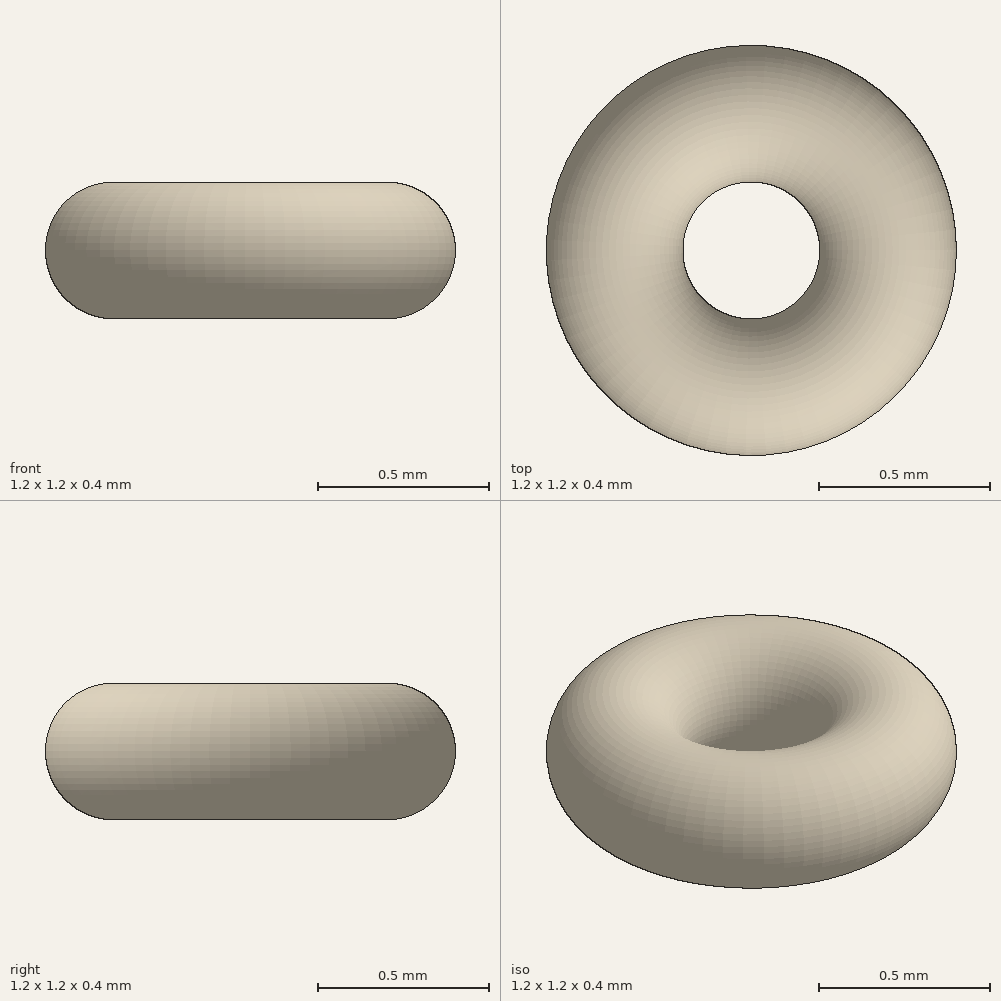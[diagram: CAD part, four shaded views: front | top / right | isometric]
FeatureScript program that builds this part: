
annotation { "Feature Type Name" : "Feature", "Feature Type Description" : "" }
export const myFeature = defineFeature(function(context is Context, id is Id, definition is map)
    precondition{}
    {
        {
            var Q0;
            Q0=qCreatedBy(makeId("Top.planeOp"),FACE);
            cPlane(context, id + "F0", {"entities" : qUnion([Q0]), "cplaneType" : CPlaneType.OFFSET, "offset" : 0.2 * mm, "width" : 150 * mm, "height" : 150 * mm});
        }
        {
            var Q0;
            Q0=qCreatedBy(id+"F0.planeOp",FACE);
            var sketch = newSketch(context, id + "F1", { "sketchPlane" : qUnion([Q0])});
            skLineSegment(sketch, "E0.bottom", {"start": v(10, 10) * mm, "end": v(-10, 10) * mm});
            skLineSegment(sketch, "E0.top", {"start": v(10, -10) * mm, "end": v(-10, -10) * mm});
            skLineSegment(sketch, "E0.right", {"start": v(-10, 9.6) * mm, "end": v(-10, -10) * mm});
            skPoint(sketch, "E0.middle", {"position": v(0, 0) * mm});
            skLineSegment(sketch, "E1", {"start": v(-9.6, 10) * mm, "end": v(-9.6, 10) * mm});
            skLineSegment(sketch, "E2", {"start": v(-9.2, 9.6) * mm, "end": v(-9.2, -9.6) * mm});
            skLineSegment(sketch, "E3", {"start": v(-9.2, -10) * mm, "end": v(-10, -10) * mm});
            skLineSegment(sketch, "E4", {"start": v(-9.2, 10) * mm, "end": v(-8.4, 10) * mm});
            skLineSegment(sketch, "E5", {"start": v(-8.4, 10) * mm, "end": v(-8.4, -9.6) * mm});
            skLineSegment(sketch, "E6", {"start": v(-8.8, -10) * mm, "end": v(-8.8, -10) * mm});
            skPoint(sketch, "E7.visualSharp", {"position": v(-10, 10) * mm});
            skArc(sketch, "E7.filletArc", {"start": v(-9.6, 10) * mm, "mid": v(-9.88, 9.88) * mm, "end": v(-10, 9.6) * mm});
            skPoint(sketch, "E8.visualSharp", {"position": v(-9.2, 10) * mm});
            skArc(sketch, "E8.filletArc", {"start": v(-9.2, 9.6) * mm, "mid": v(-9.32, 9.88) * mm, "end": v(-9.6, 10) * mm});
            skPoint(sketch, "E9.visualSharp", {"position": v(-9.2, -10) * mm});
            skArc(sketch, "E9.filletArc", {"start": v(-9.2, -9.6) * mm, "mid": v(-9.08, -9.88) * mm, "end": v(-8.8, -10) * mm});
            skPoint(sketch, "E10.visualSharp", {"position": v(-8.4, -10) * mm});
            skArc(sketch, "E10.filletArc", {"start": v(-8.8, -10) * mm, "mid": v(-8.52, -9.88) * mm, "end": v(-8.4, -9.6) * mm});
            skLineSegment(sketch, "E11", {"start": v(-8.4, 9.6) * mm, "end": v(-8.4, -9.6) * mm});
            skArc(sketch, "E12.1.0.0", {"start": v(-8, 10) * mm, "mid": v(-8.28, 9.88) * mm, "end": v(-8.4, 9.6) * mm});
            skArc(sketch, "E12.1.0.1", {"start": v(-7.6, 9.6) * mm, "mid": v(-7.72, 9.88) * mm, "end": v(-8, 10) * mm});
            skLineSegment(sketch, "E12.1.0.2", {"start": v(-7.6, 9.6) * mm, "end": v(-7.6, -9.6) * mm});
            skArc(sketch, "E12.1.0.3", {"start": v(-7.6, -9.6) * mm, "mid": v(-7.48, -9.88) * mm, "end": v(-7.2, -10) * mm});
            skArc(sketch, "E12.1.0.4", {"start": v(-7.2, -10) * mm, "mid": v(-6.92, -9.88) * mm, "end": v(-6.8, -9.6) * mm});
            skLineSegment(sketch, "E12.1.0.5", {"start": v(-6.8, 9.6) * mm, "end": v(-6.8, -9.6) * mm});
            skArc(sketch, "E12.2.0.0", {"start": v(-6.4, 10) * mm, "mid": v(-6.68, 9.88) * mm, "end": v(-6.8, 9.6) * mm});
            skArc(sketch, "E12.2.0.1", {"start": v(-6, 9.6) * mm, "mid": v(-6.12, 9.88) * mm, "end": v(-6.4, 10) * mm});
            skLineSegment(sketch, "E12.2.0.2", {"start": v(-6, 9.6) * mm, "end": v(-6, -9.6) * mm});
            skArc(sketch, "E12.2.0.3", {"start": v(-6, -9.6) * mm, "mid": v(-5.88, -9.88) * mm, "end": v(-5.6, -10) * mm});
            skArc(sketch, "E12.2.0.4", {"start": v(-5.6, -10) * mm, "mid": v(-5.32, -9.88) * mm, "end": v(-5.2, -9.6) * mm});
            skLineSegment(sketch, "E12.2.0.5", {"start": v(-5.2, 9.6) * mm, "end": v(-5.2, -9.6) * mm});
            skArc(sketch, "E12.3.0.0", {"start": v(-4.8, 10) * mm, "mid": v(-5.08, 9.88) * mm, "end": v(-5.2, 9.6) * mm});
            skArc(sketch, "E12.3.0.1", {"start": v(-4.4, 9.6) * mm, "mid": v(-4.52, 9.88) * mm, "end": v(-4.8, 10) * mm});
            skLineSegment(sketch, "E12.3.0.2", {"start": v(-4.4, 9.6) * mm, "end": v(-4.4, -9.6) * mm});
            skArc(sketch, "E12.3.0.3", {"start": v(-4.4, -9.6) * mm, "mid": v(-4.28, -9.88) * mm, "end": v(-4, -10) * mm});
            skArc(sketch, "E12.3.0.4", {"start": v(-4, -10) * mm, "mid": v(-3.72, -9.88) * mm, "end": v(-3.6, -9.6) * mm});
            skLineSegment(sketch, "E12.3.0.5", {"start": v(-3.6, 9.6) * mm, "end": v(-3.6, -9.6) * mm});
            skArc(sketch, "E12.4.0.0", {"start": v(-3.2, 10) * mm, "mid": v(-3.48, 9.88) * mm, "end": v(-3.6, 9.6) * mm});
            skArc(sketch, "E12.4.0.1", {"start": v(-2.8, 9.6) * mm, "mid": v(-2.92, 9.88) * mm, "end": v(-3.2, 10) * mm});
            skLineSegment(sketch, "E12.4.0.2", {"start": v(-2.8, 9.6) * mm, "end": v(-2.8, -9.6) * mm});
            skArc(sketch, "E12.4.0.3", {"start": v(-2.8, -9.6) * mm, "mid": v(-2.68, -9.88) * mm, "end": v(-2.4, -10) * mm});
            skArc(sketch, "E12.4.0.4", {"start": v(-2.4, -10) * mm, "mid": v(-2.12, -9.88) * mm, "end": v(-2, -9.6) * mm});
            skLineSegment(sketch, "E12.4.0.5", {"start": v(-2, 9.6) * mm, "end": v(-2, -9.6) * mm});
            skArc(sketch, "E12.5.0.0", {"start": v(-1.6, 10) * mm, "mid": v(-1.88, 9.88) * mm, "end": v(-2, 9.6) * mm});
            skArc(sketch, "E12.5.0.1", {"start": v(-1.2, 9.6) * mm, "mid": v(-1.32, 9.88) * mm, "end": v(-1.6, 10) * mm});
            skLineSegment(sketch, "E12.5.0.2", {"start": v(-1.2, 9.6) * mm, "end": v(-1.2, -9.6) * mm});
            skArc(sketch, "E12.5.0.3", {"start": v(-1.2, -9.6) * mm, "mid": v(-1.08, -9.88) * mm, "end": v(-0.8, -10) * mm});
            skArc(sketch, "E12.5.0.4", {"start": v(-0.8, -10) * mm, "mid": v(-0.52, -9.88) * mm, "end": v(-0.4, -9.6) * mm});
            skLineSegment(sketch, "E12.5.0.5", {"start": v(-0.4, 9.6) * mm, "end": v(-0.4, -9.6) * mm});
            skArc(sketch, "E12.6.0.0", {"start": v(0, 10) * mm, "mid": v(-0.28, 9.88) * mm, "end": v(-0.4, 9.6) * mm});
            skArc(sketch, "E12.6.0.1", {"start": v(0.4, 9.6) * mm, "mid": v(0.28, 9.88) * mm, "end": v(0, 10) * mm});
            skLineSegment(sketch, "E12.6.0.2", {"start": v(0.4, 9.6) * mm, "end": v(0.4, -9.6) * mm});
            skArc(sketch, "E12.6.0.3", {"start": v(0.4, -9.6) * mm, "mid": v(0.52, -9.88) * mm, "end": v(0.8, -10) * mm});
            skArc(sketch, "E12.6.0.4", {"start": v(0.8, -10) * mm, "mid": v(1.08, -9.88) * mm, "end": v(1.2, -9.6) * mm});
            skLineSegment(sketch, "E12.6.0.5", {"start": v(1.2, 9.6) * mm, "end": v(1.2, -9.6) * mm});
            skArc(sketch, "E12.7.0.0", {"start": v(1.6, 10) * mm, "mid": v(1.32, 9.88) * mm, "end": v(1.2, 9.6) * mm});
            skArc(sketch, "E12.7.0.1", {"start": v(2, 9.6) * mm, "mid": v(1.88, 9.88) * mm, "end": v(1.6, 10) * mm});
            skLineSegment(sketch, "E12.7.0.2", {"start": v(2, 9.6) * mm, "end": v(2, -9.6) * mm});
            skArc(sketch, "E12.7.0.3", {"start": v(2, -9.6) * mm, "mid": v(2.12, -9.88) * mm, "end": v(2.4, -10) * mm});
            skArc(sketch, "E12.7.0.4", {"start": v(2.4, -10) * mm, "mid": v(2.68, -9.88) * mm, "end": v(2.8, -9.6) * mm});
            skLineSegment(sketch, "E12.7.0.5", {"start": v(2.8, 9.6) * mm, "end": v(2.8, -9.6) * mm});
            skArc(sketch, "E12.8.0.0", {"start": v(3.2, 10) * mm, "mid": v(2.92, 9.88) * mm, "end": v(2.8, 9.6) * mm});
            skArc(sketch, "E12.8.0.1", {"start": v(3.6, 9.6) * mm, "mid": v(3.48, 9.88) * mm, "end": v(3.2, 10) * mm});
            skLineSegment(sketch, "E12.8.0.2", {"start": v(3.6, 9.6) * mm, "end": v(3.6, -9.6) * mm});
            skArc(sketch, "E12.8.0.3", {"start": v(3.6, -9.6) * mm, "mid": v(3.72, -9.88) * mm, "end": v(4, -10) * mm});
            skArc(sketch, "E12.8.0.4", {"start": v(4, -10) * mm, "mid": v(4.28, -9.88) * mm, "end": v(4.4, -9.6) * mm});
            skLineSegment(sketch, "E12.8.0.5", {"start": v(4.4, 9.6) * mm, "end": v(4.4, -9.6) * mm});
            skArc(sketch, "E12.9.0.0", {"start": v(4.8, 10) * mm, "mid": v(4.52, 9.88) * mm, "end": v(4.4, 9.6) * mm});
            skArc(sketch, "E12.9.0.1", {"start": v(5.2, 9.6) * mm, "mid": v(5.08, 9.88) * mm, "end": v(4.8, 10) * mm});
            skLineSegment(sketch, "E12.9.0.2", {"start": v(5.2, 9.6) * mm, "end": v(5.2, -9.6) * mm});
            skArc(sketch, "E12.9.0.3", {"start": v(5.2, -9.6) * mm, "mid": v(5.32, -9.88) * mm, "end": v(5.6, -10) * mm});
            skArc(sketch, "E12.9.0.4", {"start": v(5.6, -10) * mm, "mid": v(5.88, -9.88) * mm, "end": v(6, -9.6) * mm});
            skLineSegment(sketch, "E12.9.0.5", {"start": v(6, 9.6) * mm, "end": v(6, -9.6) * mm});
            skArc(sketch, "E12.10.0.0", {"start": v(6.4, 10) * mm, "mid": v(6.12, 9.88) * mm, "end": v(6, 9.6) * mm});
            skArc(sketch, "E12.10.0.1", {"start": v(6.8, 9.6) * mm, "mid": v(6.68, 9.88) * mm, "end": v(6.4, 10) * mm});
            skLineSegment(sketch, "E12.10.0.2", {"start": v(6.8, 9.6) * mm, "end": v(6.8, -9.6) * mm});
            skArc(sketch, "E12.10.0.3", {"start": v(6.8, -9.6) * mm, "mid": v(6.92, -9.88) * mm, "end": v(7.2, -10) * mm});
            skArc(sketch, "E12.10.0.4", {"start": v(7.2, -10) * mm, "mid": v(7.48, -9.88) * mm, "end": v(7.6, -9.6) * mm});
            skLineSegment(sketch, "E12.10.0.5", {"start": v(7.6, 9.6) * mm, "end": v(7.6, -9.6) * mm});
            skArc(sketch, "E12.11.0.0", {"start": v(8, 10) * mm, "mid": v(7.72, 9.88) * mm, "end": v(7.6, 9.6) * mm});
            skArc(sketch, "E12.11.0.1", {"start": v(8.4, 9.6) * mm, "mid": v(8.28, 9.88) * mm, "end": v(8, 10) * mm});
            skLineSegment(sketch, "E12.11.0.2", {"start": v(8.4, 9.6) * mm, "end": v(8.4, -9.6) * mm});
            skArc(sketch, "E12.11.0.3", {"start": v(8.4, -9.6) * mm, "mid": v(8.52, -9.88) * mm, "end": v(8.8, -10) * mm});
            skArc(sketch, "E12.11.0.4", {"start": v(8.8, -10) * mm, "mid": v(9.08, -9.88) * mm, "end": v(9.2, -9.6) * mm});
            skLineSegment(sketch, "E12.11.0.5", {"start": v(9.2, 9.6) * mm, "end": v(9.2, -9.6) * mm});
            skLineSegment(sketch, "E12.direction1", {"start": v(-8.8, -10) * mm, "end": v(-7.2, -10) * mm, "construction": true});
            skLineSegment(sketch, "E13", {"start": v(10, 10) * mm, "end": v(9.6, 10) * mm});
            skLineSegment(sketch, "E14", {"start": v(10, 10) * mm, "end": v(10, 9.6) * mm});
            skArc(sketch, "E15", {"start": v(9.2, 9.6) * mm, "mid": v(9.6, 10) * mm, "end": v(10, 9.6) * mm});
            skLineSegment(sketch, "E16", {"start": v(10, -10) * mm, "end": v(10, -8.4) * mm});
            skLineSegment(sketch, "E17", {"start": v(10, -8.4) * mm, "end": v(10, 9.6) * mm});
            skLineSegment(sketch, "E18", {"start": v(-10, 9.6) * mm, "end": v(-10, -11.6) * mm});
            skSolve(sketch);
        }
        {
            var Q0;
            Q0=qCreatedBy(id+"F0.planeOp",FACE);
            cPlane(context, id + "F2", {"entities" : qUnion([Q0]), "cplaneType" : CPlaneType.OFFSET, "offset" : 0.4 * mm, "width" : 150 * mm, "height" : 150 * mm});
        }
        {
            var Q0;
            Q0=qCreatedBy(id+"F2.planeOp",FACE);
            var sketch = newSketch(context, id + "F3", { "sketchPlane" : qUnion([Q0])});
            skLineSegment(sketch, "E19.top", {"start": v(8.4, -8.4) * mm, "end": v(-8, -8.4) * mm});
            skLineSegment(sketch, "E19.left", {"start": v(8.4, 8.4) * mm, "end": v(8.4, -8.4) * mm});
            skLineSegment(sketch, "E19.right", {"start": v(-8.4, 8.4) * mm, "end": v(-8.4, -8.4) * mm});
            skPoint(sketch, "E19.middle", {"position": v(0, 0) * mm});
            skLineSegment(sketch, "E20", {"start": v(-8.4, -8) * mm, "end": v(-8.4, -8) * mm});
            skLineSegment(sketch, "E21", {"start": v(-8, -7.6) * mm, "end": v(8, -7.6) * mm});
            skLineSegment(sketch, "E22", {"start": v(8.4, -7.6) * mm, "end": v(8.4, -8.4) * mm});
            skLineSegment(sketch, "E23", {"start": v(-8.4, -7.6) * mm, "end": v(-8.4, -6.8) * mm});
            skLineSegment(sketch, "E24", {"start": v(-8.4, -6.8) * mm, "end": v(8, -6.8) * mm});
            skLineSegment(sketch, "E25", {"start": v(8.4, -7.2) * mm, "end": v(8.4, -7.2) * mm});
            skPoint(sketch, "E26.visualSharp", {"position": v(-8.4, -8.4) * mm});
            skArc(sketch, "E26.filletArc", {"start": v(-8.4, -8) * mm, "mid": v(-8.28, -8.28) * mm, "end": v(-8, -8.4) * mm});
            skPoint(sketch, "E27.visualSharp", {"position": v(-8.4, -7.6) * mm});
            skArc(sketch, "E27.filletArc", {"start": v(-8, -7.6) * mm, "mid": v(-8.28, -7.72) * mm, "end": v(-8.4, -8) * mm});
            skPoint(sketch, "E28.visualSharp", {"position": v(8.4, -7.6) * mm});
            skArc(sketch, "E28.filletArc", {"start": v(8, -7.6) * mm, "mid": v(8.28, -7.48) * mm, "end": v(8.4, -7.2) * mm});
            skPoint(sketch, "E29.visualSharp", {"position": v(8.4, -6.8) * mm});
            skArc(sketch, "E29.filletArc", {"start": v(8.4, -7.2) * mm, "mid": v(8.28, -6.92) * mm, "end": v(8, -6.8) * mm});
            skLineSegment(sketch, "E30", {"start": v(-8, -6.8) * mm, "end": v(8, -6.8) * mm});
            skArc(sketch, "E31.1.0.0", {"start": v(-8.4, -6.4) * mm, "mid": v(-8.28, -6.68) * mm, "end": v(-8, -6.8) * mm});
            skArc(sketch, "E31.1.0.1", {"start": v(-8, -6) * mm, "mid": v(-8.28, -6.12) * mm, "end": v(-8.4, -6.4) * mm});
            skLineSegment(sketch, "E31.1.0.2", {"start": v(-8, -6) * mm, "end": v(8, -6) * mm});
            skArc(sketch, "E31.1.0.3", {"start": v(8, -6) * mm, "mid": v(8.28, -5.88) * mm, "end": v(8.4, -5.6) * mm});
            skArc(sketch, "E31.1.0.4", {"start": v(8.4, -5.6) * mm, "mid": v(8.28, -5.32) * mm, "end": v(8, -5.2) * mm});
            skLineSegment(sketch, "E31.1.0.5", {"start": v(-8, -5.2) * mm, "end": v(8, -5.2) * mm});
            skArc(sketch, "E31.2.0.0", {"start": v(-8.4, -4.8) * mm, "mid": v(-8.28, -5.08) * mm, "end": v(-8, -5.2) * mm});
            skArc(sketch, "E31.2.0.1", {"start": v(-8, -4.4) * mm, "mid": v(-8.28, -4.52) * mm, "end": v(-8.4, -4.8) * mm});
            skLineSegment(sketch, "E31.2.0.2", {"start": v(-8, -4.4) * mm, "end": v(8, -4.4) * mm});
            skArc(sketch, "E31.2.0.3", {"start": v(8, -4.4) * mm, "mid": v(8.28, -4.28) * mm, "end": v(8.4, -4) * mm});
            skArc(sketch, "E31.2.0.4", {"start": v(8.4, -4) * mm, "mid": v(8.28, -3.72) * mm, "end": v(8, -3.6) * mm});
            skLineSegment(sketch, "E31.2.0.5", {"start": v(-8, -3.6) * mm, "end": v(8, -3.6) * mm});
            skArc(sketch, "E31.3.0.0", {"start": v(-8.4, -3.2) * mm, "mid": v(-8.28, -3.48) * mm, "end": v(-8, -3.6) * mm});
            skArc(sketch, "E31.3.0.1", {"start": v(-8, -2.8) * mm, "mid": v(-8.28, -2.92) * mm, "end": v(-8.4, -3.2) * mm});
            skLineSegment(sketch, "E31.3.0.2", {"start": v(-8, -2.8) * mm, "end": v(8, -2.8) * mm});
            skArc(sketch, "E31.3.0.3", {"start": v(8, -2.8) * mm, "mid": v(8.28, -2.68) * mm, "end": v(8.4, -2.4) * mm});
            skArc(sketch, "E31.3.0.4", {"start": v(8.4, -2.4) * mm, "mid": v(8.28, -2.12) * mm, "end": v(8, -2) * mm});
            skLineSegment(sketch, "E31.3.0.5", {"start": v(-8, -2) * mm, "end": v(8, -2) * mm});
            skArc(sketch, "E31.4.0.0", {"start": v(-8.4, -1.6) * mm, "mid": v(-8.28, -1.88) * mm, "end": v(-8, -2) * mm});
            skArc(sketch, "E31.4.0.1", {"start": v(-8, -1.2) * mm, "mid": v(-8.28, -1.32) * mm, "end": v(-8.4, -1.6) * mm});
            skLineSegment(sketch, "E31.4.0.2", {"start": v(-8, -1.2) * mm, "end": v(8, -1.2) * mm});
            skArc(sketch, "E31.4.0.3", {"start": v(8, -1.2) * mm, "mid": v(8.28, -1.08) * mm, "end": v(8.4, -0.8) * mm});
            skArc(sketch, "E31.4.0.4", {"start": v(8.4, -0.8) * mm, "mid": v(8.28, -0.52) * mm, "end": v(8, -0.4) * mm});
            skLineSegment(sketch, "E31.4.0.5", {"start": v(-8, -0.4) * mm, "end": v(8, -0.4) * mm});
            skArc(sketch, "E31.5.0.0", {"start": v(-8.4, 0) * mm, "mid": v(-8.28, -0.28) * mm, "end": v(-8, -0.4) * mm});
            skArc(sketch, "E31.5.0.1", {"start": v(-8, 0.4) * mm, "mid": v(-8.28, 0.28) * mm, "end": v(-8.4, 0) * mm});
            skLineSegment(sketch, "E31.5.0.2", {"start": v(-8, 0.4) * mm, "end": v(8, 0.4) * mm});
            skArc(sketch, "E31.5.0.3", {"start": v(8, 0.4) * mm, "mid": v(8.28, 0.52) * mm, "end": v(8.4, 0.8) * mm});
            skArc(sketch, "E31.5.0.4", {"start": v(8.4, 0.8) * mm, "mid": v(8.28, 1.08) * mm, "end": v(8, 1.2) * mm});
            skLineSegment(sketch, "E31.5.0.5", {"start": v(-8, 1.2) * mm, "end": v(8, 1.2) * mm});
            skArc(sketch, "E31.6.0.0", {"start": v(-8.4, 1.6) * mm, "mid": v(-8.28, 1.32) * mm, "end": v(-8, 1.2) * mm});
            skArc(sketch, "E31.6.0.1", {"start": v(-8, 2) * mm, "mid": v(-8.28, 1.88) * mm, "end": v(-8.4, 1.6) * mm});
            skLineSegment(sketch, "E31.6.0.2", {"start": v(-8, 2) * mm, "end": v(8, 2) * mm});
            skArc(sketch, "E31.6.0.3", {"start": v(8, 2) * mm, "mid": v(8.28, 2.12) * mm, "end": v(8.4, 2.4) * mm});
            skArc(sketch, "E31.6.0.4", {"start": v(8.4, 2.4) * mm, "mid": v(8.28, 2.68) * mm, "end": v(8, 2.8) * mm});
            skLineSegment(sketch, "E31.6.0.5", {"start": v(-8, 2.8) * mm, "end": v(8, 2.8) * mm});
            skArc(sketch, "E31.7.0.0", {"start": v(-8.4, 3.2) * mm, "mid": v(-8.28, 2.92) * mm, "end": v(-8, 2.8) * mm});
            skArc(sketch, "E31.7.0.1", {"start": v(-8, 3.6) * mm, "mid": v(-8.28, 3.48) * mm, "end": v(-8.4, 3.2) * mm});
            skLineSegment(sketch, "E31.7.0.2", {"start": v(-8, 3.6) * mm, "end": v(8, 3.6) * mm});
            skArc(sketch, "E31.7.0.3", {"start": v(8, 3.6) * mm, "mid": v(8.28, 3.72) * mm, "end": v(8.4, 4) * mm});
            skArc(sketch, "E31.7.0.4", {"start": v(8.4, 4) * mm, "mid": v(8.28, 4.28) * mm, "end": v(8, 4.4) * mm});
            skLineSegment(sketch, "E31.7.0.5", {"start": v(-8, 4.4) * mm, "end": v(8, 4.4) * mm});
            skArc(sketch, "E31.8.0.0", {"start": v(-8.4, 4.8) * mm, "mid": v(-8.28, 4.52) * mm, "end": v(-8, 4.4) * mm});
            skArc(sketch, "E31.8.0.1", {"start": v(-8, 5.2) * mm, "mid": v(-8.28, 5.08) * mm, "end": v(-8.4, 4.8) * mm});
            skLineSegment(sketch, "E31.8.0.2", {"start": v(-8, 5.2) * mm, "end": v(8, 5.2) * mm});
            skArc(sketch, "E31.8.0.3", {"start": v(8, 5.2) * mm, "mid": v(8.28, 5.32) * mm, "end": v(8.4, 5.6) * mm});
            skArc(sketch, "E31.8.0.4", {"start": v(8.4, 5.6) * mm, "mid": v(8.28, 5.88) * mm, "end": v(8, 6) * mm});
            skLineSegment(sketch, "E31.8.0.5", {"start": v(-8, 6) * mm, "end": v(8, 6) * mm});
            skArc(sketch, "E31.9.0.0", {"start": v(-8.4, 6.4) * mm, "mid": v(-8.28, 6.12) * mm, "end": v(-8, 6) * mm});
            skArc(sketch, "E31.9.0.1", {"start": v(-8, 6.8) * mm, "mid": v(-8.28, 6.68) * mm, "end": v(-8.4, 6.4) * mm});
            skLineSegment(sketch, "E31.9.0.2", {"start": v(-8, 6.8) * mm, "end": v(8, 6.8) * mm});
            skArc(sketch, "E31.9.0.3", {"start": v(8, 6.8) * mm, "mid": v(8.28, 6.92) * mm, "end": v(8.4, 7.2) * mm});
            skArc(sketch, "E31.9.0.4", {"start": v(8.4, 7.2) * mm, "mid": v(8.28, 7.48) * mm, "end": v(8, 7.6) * mm});
            skLineSegment(sketch, "E31.9.0.5", {"start": v(-8, 7.6) * mm, "end": v(8, 7.6) * mm});
            skLineSegment(sketch, "E31.direction1", {"start": v(-8, -8.4) * mm, "end": v(-8, -6.8) * mm, "construction": true});
            skLineSegment(sketch, "E32", {"start": v(-8.4, 8.4) * mm, "end": v(-8.4, 8) * mm});
            skLineSegment(sketch, "E33", {"start": v(-8.4, 8.4) * mm, "end": v(-8, 8.4) * mm});
            skArc(sketch, "E34", {"start": v(-8, 7.6) * mm, "mid": v(-8.4, 8) * mm, "end": v(-8, 8.4) * mm});
            skLineSegment(sketch, "E35", {"start": v(8, 8.4) * mm, "end": v(-8, 8.4) * mm});
            skLineSegment(sketch, "E36", {"start": v(-8, -8.4) * mm, "end": v(10, -8.4) * mm});
            skLineSegment(sketch, "E37", {"start": v(8.4, 8.4) * mm, "end": v(6.8, 8.4) * mm});
            skLineSegment(sketch, "E38", {"start": v(6.8, 8.4) * mm, "end": v(-8, 8.4) * mm});
            skSolve(sketch);
        }
        {
            var Q0;
            Q0=qCreatedBy(id+"F2.planeOp",FACE);
            cPlane(context, id + "F4", {"entities" : qUnion([Q0]), "cplaneType" : CPlaneType.OFFSET, "offset" : 0.4 * mm, "width" : 150 * mm, "height" : 150 * mm});
        }
        {
            var Q0;
            Q0=qCreatedBy(id+"F4.planeOp",FACE);
            var sketch = newSketch(context, id + "F5", { "sketchPlane" : qUnion([Q0])});
            skLineSegment(sketch, "E39.bottom", {"start": v(6.8, 6.8) * mm, "end": v(-6.8, 6.8) * mm});
            skLineSegment(sketch, "E39.top", {"start": v(6.8, -6.8) * mm, "end": v(-6.8, -6.8) * mm});
            skLineSegment(sketch, "E39.left", {"start": v(6.8, 6.8) * mm, "end": v(6.8, -6.4) * mm});
            skPoint(sketch, "E39.middle", {"position": v(0, 0) * mm});
            skLineSegment(sketch, "E40", {"start": v(6.8, 6.8) * mm, "end": v(6, 6.8) * mm});
            skLineSegment(sketch, "E41", {"start": v(6, 6.4) * mm, "end": v(6, -6.4) * mm});
            skLineSegment(sketch, "E42", {"start": v(6.4, -6.8) * mm, "end": v(6.4, -6.8) * mm});
            skLineSegment(sketch, "E43", {"start": v(5.6, 6.8) * mm, "end": v(5.6, 6.8) * mm});
            skLineSegment(sketch, "E44", {"start": v(5.2, 6.4) * mm, "end": v(5.2, -6.8) * mm});
            skLineSegment(sketch, "E45", {"start": v(5.2, -6.8) * mm, "end": v(6, -6.8) * mm});
            skPoint(sketch, "E46.visualSharp", {"position": v(6.8, -6.8) * mm});
            skArc(sketch, "E46.filletArc", {"start": v(6.4, -6.8) * mm, "mid": v(6.68, -6.68) * mm, "end": v(6.8, -6.4) * mm});
            skPoint(sketch, "E47.visualSharp", {"position": v(6, -6.8) * mm});
            skArc(sketch, "E47.filletArc", {"start": v(6, -6.4) * mm, "mid": v(6.12, -6.68) * mm, "end": v(6.4, -6.8) * mm});
            skPoint(sketch, "E48.visualSharp", {"position": v(6, 6.8) * mm});
            skArc(sketch, "E48.filletArc", {"start": v(6, 6.4) * mm, "mid": v(5.88, 6.68) * mm, "end": v(5.6, 6.8) * mm});
            skPoint(sketch, "E49.visualSharp", {"position": v(5.2, 6.8) * mm});
            skArc(sketch, "E49.filletArc", {"start": v(5.6, 6.8) * mm, "mid": v(5.32, 6.68) * mm, "end": v(5.2, 6.4) * mm});
            skLineSegment(sketch, "E50", {"start": v(5.2, -6.4) * mm, "end": v(5.2, 6.4) * mm});
            skArc(sketch, "E51.1.0.0", {"start": v(4.8, -6.8) * mm, "mid": v(5.08, -6.68) * mm, "end": v(5.2, -6.4) * mm});
            skArc(sketch, "E51.1.0.1", {"start": v(4.4, -6.4) * mm, "mid": v(4.52, -6.68) * mm, "end": v(4.8, -6.8) * mm});
            skLineSegment(sketch, "E51.1.0.2", {"start": v(4.4, 6.4) * mm, "end": v(4.4, -6.4) * mm});
            skArc(sketch, "E51.1.0.3", {"start": v(4.4, 6.4) * mm, "mid": v(4.28, 6.68) * mm, "end": v(4, 6.8) * mm});
            skArc(sketch, "E51.1.0.4", {"start": v(4, 6.8) * mm, "mid": v(3.72, 6.68) * mm, "end": v(3.6, 6.4) * mm});
            skLineSegment(sketch, "E51.1.0.5", {"start": v(3.6, -6.4) * mm, "end": v(3.6, 6.4) * mm});
            skArc(sketch, "E51.2.0.0", {"start": v(3.2, -6.8) * mm, "mid": v(3.48, -6.68) * mm, "end": v(3.6, -6.4) * mm});
            skArc(sketch, "E51.2.0.1", {"start": v(2.8, -6.4) * mm, "mid": v(2.92, -6.68) * mm, "end": v(3.2, -6.8) * mm});
            skLineSegment(sketch, "E51.2.0.2", {"start": v(2.8, 6.4) * mm, "end": v(2.8, -6.4) * mm});
            skArc(sketch, "E51.2.0.3", {"start": v(2.8, 6.4) * mm, "mid": v(2.68, 6.68) * mm, "end": v(2.4, 6.8) * mm});
            skArc(sketch, "E51.2.0.4", {"start": v(2.4, 6.8) * mm, "mid": v(2.12, 6.68) * mm, "end": v(2, 6.4) * mm});
            skLineSegment(sketch, "E51.2.0.5", {"start": v(2, -6.4) * mm, "end": v(2, 6.4) * mm});
            skArc(sketch, "E51.3.0.0", {"start": v(1.6, -6.8) * mm, "mid": v(1.88, -6.68) * mm, "end": v(2, -6.4) * mm});
            skArc(sketch, "E51.3.0.1", {"start": v(1.2, -6.4) * mm, "mid": v(1.32, -6.68) * mm, "end": v(1.6, -6.8) * mm});
            skLineSegment(sketch, "E51.3.0.2", {"start": v(1.2, 6.4) * mm, "end": v(1.2, -6.4) * mm});
            skArc(sketch, "E51.3.0.3", {"start": v(1.2, 6.4) * mm, "mid": v(1.08, 6.68) * mm, "end": v(0.8, 6.8) * mm});
            skArc(sketch, "E51.3.0.4", {"start": v(0.8, 6.8) * mm, "mid": v(0.52, 6.68) * mm, "end": v(0.4, 6.4) * mm});
            skLineSegment(sketch, "E51.3.0.5", {"start": v(0.4, -6.4) * mm, "end": v(0.4, 6.4) * mm});
            skArc(sketch, "E51.4.0.0", {"start": v(0, -6.8) * mm, "mid": v(0.28, -6.68) * mm, "end": v(0.4, -6.4) * mm});
            skArc(sketch, "E51.4.0.1", {"start": v(-0.4, -6.4) * mm, "mid": v(-0.28, -6.68) * mm, "end": v(0, -6.8) * mm});
            skLineSegment(sketch, "E51.4.0.2", {"start": v(-0.4, 6.4) * mm, "end": v(-0.4, -6.4) * mm});
            skArc(sketch, "E51.4.0.3", {"start": v(-0.4, 6.4) * mm, "mid": v(-0.52, 6.68) * mm, "end": v(-0.8, 6.8) * mm});
            skArc(sketch, "E51.4.0.4", {"start": v(-0.8, 6.8) * mm, "mid": v(-1.08, 6.68) * mm, "end": v(-1.2, 6.4) * mm});
            skLineSegment(sketch, "E51.4.0.5", {"start": v(-1.2, -6.4) * mm, "end": v(-1.2, 6.4) * mm});
            skArc(sketch, "E51.5.0.0", {"start": v(-1.6, -6.8) * mm, "mid": v(-1.32, -6.68) * mm, "end": v(-1.2, -6.4) * mm});
            skArc(sketch, "E51.5.0.1", {"start": v(-2, -6.4) * mm, "mid": v(-1.88, -6.68) * mm, "end": v(-1.6, -6.8) * mm});
            skLineSegment(sketch, "E51.5.0.2", {"start": v(-2, 6.4) * mm, "end": v(-2, -6.4) * mm});
            skArc(sketch, "E51.5.0.3", {"start": v(-2, 6.4) * mm, "mid": v(-2.12, 6.68) * mm, "end": v(-2.4, 6.8) * mm});
            skArc(sketch, "E51.5.0.4", {"start": v(-2.4, 6.8) * mm, "mid": v(-2.68, 6.68) * mm, "end": v(-2.8, 6.4) * mm});
            skLineSegment(sketch, "E51.5.0.5", {"start": v(-2.8, -6.4) * mm, "end": v(-2.8, 6.4) * mm});
            skArc(sketch, "E51.6.0.0", {"start": v(-3.2, -6.8) * mm, "mid": v(-2.92, -6.68) * mm, "end": v(-2.8, -6.4) * mm});
            skArc(sketch, "E51.6.0.1", {"start": v(-3.6, -6.4) * mm, "mid": v(-3.48, -6.68) * mm, "end": v(-3.2, -6.8) * mm});
            skLineSegment(sketch, "E51.6.0.2", {"start": v(-3.6, 6.4) * mm, "end": v(-3.6, -6.4) * mm});
            skArc(sketch, "E51.6.0.3", {"start": v(-3.6, 6.4) * mm, "mid": v(-3.72, 6.68) * mm, "end": v(-4, 6.8) * mm});
            skArc(sketch, "E51.6.0.4", {"start": v(-4, 6.8) * mm, "mid": v(-4.28, 6.68) * mm, "end": v(-4.4, 6.4) * mm});
            skLineSegment(sketch, "E51.6.0.5", {"start": v(-4.4, -6.4) * mm, "end": v(-4.4, 6.4) * mm});
            skArc(sketch, "E51.7.0.0", {"start": v(-4.8, -6.8) * mm, "mid": v(-4.52, -6.68) * mm, "end": v(-4.4, -6.4) * mm});
            skArc(sketch, "E51.7.0.1", {"start": v(-5.2, -6.4) * mm, "mid": v(-5.08, -6.68) * mm, "end": v(-4.8, -6.8) * mm});
            skLineSegment(sketch, "E51.7.0.2", {"start": v(-5.2, 6.4) * mm, "end": v(-5.2, -6.4) * mm});
            skArc(sketch, "E51.7.0.3", {"start": v(-5.2, 6.4) * mm, "mid": v(-5.32, 6.68) * mm, "end": v(-5.6, 6.8) * mm});
            skArc(sketch, "E51.7.0.4", {"start": v(-5.6, 6.8) * mm, "mid": v(-5.88, 6.68) * mm, "end": v(-6, 6.4) * mm});
            skLineSegment(sketch, "E51.7.0.5", {"start": v(-6, -6.4) * mm, "end": v(-6, 6.4) * mm});
            skLineSegment(sketch, "E51.direction1", {"start": v(5.2, -6.4) * mm, "end": v(3.6, -6.4) * mm, "construction": true});
            skLineSegment(sketch, "E52", {"start": v(-6.8, -6.8) * mm, "end": v(-6.4, -6.8) * mm});
            skLineSegment(sketch, "E53", {"start": v(-6.8, -6.8) * mm, "end": v(-6.8, -6.4) * mm});
            skArc(sketch, "E54", {"start": v(-6, -6.4) * mm, "mid": v(-6.4, -6.8) * mm, "end": v(-6.8, -6.4) * mm});
            skLineSegment(sketch, "E55", {"start": v(6.8, -6.4) * mm, "end": v(6.8, 8.4) * mm});
            skLineSegment(sketch, "E56", {"start": v(-6.8, 6.8) * mm, "end": v(-6.8, 5.2) * mm});
            skLineSegment(sketch, "E57", {"start": v(-6.8, 5.2) * mm, "end": v(-6.8, -6.4) * mm});
            skSolve(sketch);
        }
        {
            var Q0;
            Q0=qCreatedBy(id+"F4.planeOp",FACE);
            cPlane(context, id + "F6", {"entities" : qUnion([Q0]), "cplaneType" : CPlaneType.OFFSET, "offset" : 0.4 * mm, "width" : 150 * mm, "height" : 150 * mm});
        }
        {
            var Q0;
            Q0=qCreatedBy(id+"F6.planeOp",FACE);
            var sketch = newSketch(context, id + "F7", { "sketchPlane" : qUnion([Q0])});
            skLineSegment(sketch, "E58.top", {"start": v(4.8, 5.2) * mm, "end": v(-5.2, 5.2) * mm});
            skLineSegment(sketch, "E58.left", {"start": v(-5.2, 5.2) * mm, "end": v(-5.2, -5.2) * mm});
            skLineSegment(sketch, "E58.right", {"start": v(5.2, -5.2) * mm, "end": v(5.2, 5.2) * mm});
            skPoint(sketch, "E58.middle", {"position": v(0, 0) * mm});
            skLineSegment(sketch, "E59", {"start": v(-5.2, 5.2) * mm, "end": v(-5.2, 4.4) * mm});
            skLineSegment(sketch, "E60", {"start": v(-4.8, 4.4) * mm, "end": v(4.8, 4.4) * mm});
            skLineSegment(sketch, "E61", {"start": v(5.2, 4.8) * mm, "end": v(5.2, 4.8) * mm});
            skLineSegment(sketch, "E62", {"start": v(-5.2, 4) * mm, "end": v(-5.2, 4) * mm});
            skLineSegment(sketch, "E63", {"start": v(-4.8, 3.6) * mm, "end": v(5.2, 3.6) * mm});
            skLineSegment(sketch, "E64", {"start": v(5.2, 3.6) * mm, "end": v(5.2, 4.4) * mm});
            skPoint(sketch, "E65.visualSharp", {"position": v(5.2, 5.2) * mm});
            skArc(sketch, "E65.filletArc", {"start": v(5.2, 4.8) * mm, "mid": v(5.08, 5.08) * mm, "end": v(4.8, 5.2) * mm});
            skPoint(sketch, "E66.visualSharp", {"position": v(5.2, 4.4) * mm});
            skArc(sketch, "E66.filletArc", {"start": v(4.8, 4.4) * mm, "mid": v(5.08, 4.52) * mm, "end": v(5.2, 4.8) * mm});
            skPoint(sketch, "E67.visualSharp", {"position": v(-5.2, 4.4) * mm});
            skArc(sketch, "E67.filletArc", {"start": v(-4.8, 4.4) * mm, "mid": v(-5.08, 4.28) * mm, "end": v(-5.2, 4) * mm});
            skPoint(sketch, "E68.visualSharp", {"position": v(-5.2, 3.6) * mm});
            skArc(sketch, "E68.filletArc", {"start": v(-5.2, 4) * mm, "mid": v(-5.08, 3.72) * mm, "end": v(-4.8, 3.6) * mm});
            skLineSegment(sketch, "E69", {"start": v(4.8, 3.6) * mm, "end": v(-4.8, 3.6) * mm});
            skArc(sketch, "E70.1.0.0", {"start": v(5.2, 3.2) * mm, "mid": v(5.08, 3.48) * mm, "end": v(4.8, 3.6) * mm});
            skArc(sketch, "E70.1.0.1", {"start": v(4.8, 2.8) * mm, "mid": v(5.08, 2.92) * mm, "end": v(5.2, 3.2) * mm});
            skLineSegment(sketch, "E70.1.0.2", {"start": v(-4.8, 2.8) * mm, "end": v(4.8, 2.8) * mm});
            skArc(sketch, "E70.1.0.3", {"start": v(-4.8, 2.8) * mm, "mid": v(-5.08, 2.68) * mm, "end": v(-5.2, 2.4) * mm});
            skArc(sketch, "E70.1.0.4", {"start": v(-5.2, 2.4) * mm, "mid": v(-5.08, 2.12) * mm, "end": v(-4.8, 2) * mm});
            skLineSegment(sketch, "E70.1.0.5", {"start": v(4.8, 2) * mm, "end": v(-4.8, 2) * mm});
            skArc(sketch, "E70.2.0.0", {"start": v(5.2, 1.6) * mm, "mid": v(5.08, 1.88) * mm, "end": v(4.8, 2) * mm});
            skArc(sketch, "E70.2.0.1", {"start": v(4.8, 1.2) * mm, "mid": v(5.08, 1.32) * mm, "end": v(5.2, 1.6) * mm});
            skLineSegment(sketch, "E70.2.0.2", {"start": v(-4.8, 1.2) * mm, "end": v(4.8, 1.2) * mm});
            skArc(sketch, "E70.2.0.3", {"start": v(-4.8, 1.2) * mm, "mid": v(-5.08, 1.08) * mm, "end": v(-5.2, 0.8) * mm});
            skArc(sketch, "E70.2.0.4", {"start": v(-5.2, 0.8) * mm, "mid": v(-5.08, 0.52) * mm, "end": v(-4.8, 0.4) * mm});
            skLineSegment(sketch, "E70.2.0.5", {"start": v(4.8, 0.4) * mm, "end": v(-4.8, 0.4) * mm});
            skArc(sketch, "E70.3.0.0", {"start": v(5.2, 0) * mm, "mid": v(5.08, 0.28) * mm, "end": v(4.8, 0.4) * mm});
            skArc(sketch, "E70.3.0.1", {"start": v(4.8, -0.4) * mm, "mid": v(5.08, -0.28) * mm, "end": v(5.2, 0) * mm});
            skLineSegment(sketch, "E70.3.0.2", {"start": v(-4.8, -0.4) * mm, "end": v(4.8, -0.4) * mm});
            skArc(sketch, "E70.3.0.3", {"start": v(-4.8, -0.4) * mm, "mid": v(-5.08, -0.52) * mm, "end": v(-5.2, -0.8) * mm});
            skArc(sketch, "E70.3.0.4", {"start": v(-5.2, -0.8) * mm, "mid": v(-5.08, -1.08) * mm, "end": v(-4.8, -1.2) * mm});
            skLineSegment(sketch, "E70.3.0.5", {"start": v(4.8, -1.2) * mm, "end": v(-4.8, -1.2) * mm});
            skArc(sketch, "E70.4.0.0", {"start": v(5.2, -1.6) * mm, "mid": v(5.08, -1.32) * mm, "end": v(4.8, -1.2) * mm});
            skArc(sketch, "E70.4.0.1", {"start": v(4.8, -2) * mm, "mid": v(5.08, -1.88) * mm, "end": v(5.2, -1.6) * mm});
            skLineSegment(sketch, "E70.4.0.2", {"start": v(-4.8, -2) * mm, "end": v(4.8, -2) * mm});
            skArc(sketch, "E70.4.0.3", {"start": v(-4.8, -2) * mm, "mid": v(-5.08, -2.12) * mm, "end": v(-5.2, -2.4) * mm});
            skArc(sketch, "E70.4.0.4", {"start": v(-5.2, -2.4) * mm, "mid": v(-5.08, -2.68) * mm, "end": v(-4.8, -2.8) * mm});
            skLineSegment(sketch, "E70.4.0.5", {"start": v(4.8, -2.8) * mm, "end": v(-4.8, -2.8) * mm});
            skArc(sketch, "E70.5.0.0", {"start": v(5.2, -3.2) * mm, "mid": v(5.08, -2.92) * mm, "end": v(4.8, -2.8) * mm});
            skArc(sketch, "E70.5.0.1", {"start": v(4.8, -3.6) * mm, "mid": v(5.08, -3.48) * mm, "end": v(5.2, -3.2) * mm});
            skLineSegment(sketch, "E70.5.0.2", {"start": v(-4.8, -3.6) * mm, "end": v(4.8, -3.6) * mm});
            skArc(sketch, "E70.5.0.3", {"start": v(-4.8, -3.6) * mm, "mid": v(-5.08, -3.72) * mm, "end": v(-5.2, -4) * mm});
            skArc(sketch, "E70.5.0.4", {"start": v(-5.2, -4) * mm, "mid": v(-5.08, -4.28) * mm, "end": v(-4.8, -4.4) * mm});
            skLineSegment(sketch, "E70.5.0.5", {"start": v(4.8, -4.4) * mm, "end": v(-4.8, -4.4) * mm});
            skLineSegment(sketch, "E70.direction1", {"start": v(-4.8, 3.6) * mm, "end": v(-4.8, 2) * mm, "construction": true});
            skLineSegment(sketch, "E71", {"start": v(5.2, -5.2) * mm, "end": v(5.2, -4.8) * mm});
            skLineSegment(sketch, "E72", {"start": v(5.2, -5.2) * mm, "end": v(4.8, -5.2) * mm});
            skArc(sketch, "E73", {"start": v(4.8, -4.4) * mm, "mid": v(5.2, -4.8) * mm, "end": v(4.8, -5.2) * mm});
            skLineSegment(sketch, "E74", {"start": v(-5.2, -5.2) * mm, "end": v(-3.6, -5.2) * mm});
            skLineSegment(sketch, "E75", {"start": v(-3.6, -5.2) * mm, "end": v(4.8, -5.2) * mm});
            skLineSegment(sketch, "E76", {"start": v(4.8, 5.2) * mm, "end": v(-6.8, 5.2) * mm});
            skSolve(sketch);
        }
        {
            var Q0;
            Q0=qCreatedBy(id+"F6.planeOp",FACE);
            cPlane(context, id + "F8", {"entities" : qUnion([Q0]), "cplaneType" : CPlaneType.OFFSET, "offset" : 0.4 * mm, "width" : 150 * mm, "height" : 150 * mm});
        }
        {
            var Q0;
            Q0=qCreatedBy(id+"F8.planeOp",FACE);
            var sketch = newSketch(context, id + "F9", { "sketchPlane" : qUnion([Q0])});
            skLineSegment(sketch, "E77.bottom", {"start": v(3.6, 3.6) * mm, "end": v(-3.6, 3.6) * mm});
            skLineSegment(sketch, "E77.top", {"start": v(3.6, -3.6) * mm, "end": v(-3.6, -3.6) * mm});
            skLineSegment(sketch, "E77.left", {"start": v(3.6, 3.6) * mm, "end": v(3.6, -3.6) * mm});
            skLineSegment(sketch, "E77.right", {"start": v(-3.6, 3.2) * mm, "end": v(-3.6, -3.6) * mm});
            skPoint(sketch, "E77.middle", {"position": v(0, 0) * mm});
            skLineSegment(sketch, "E78", {"start": v(-3.2, 3.6) * mm, "end": v(-3.2, 3.6) * mm});
            skLineSegment(sketch, "E79", {"start": v(-2.8, 3.2) * mm, "end": v(-2.8, -3.2) * mm});
            skLineSegment(sketch, "E80", {"start": v(-2.8, -3.6) * mm, "end": v(-3.6, -3.6) * mm});
            skLineSegment(sketch, "E81", {"start": v(-2.8, 3.6) * mm, "end": v(-2, 3.6) * mm});
            skLineSegment(sketch, "E82", {"start": v(-2, 3.6) * mm, "end": v(-2, -3.2) * mm});
            skLineSegment(sketch, "E83", {"start": v(-2.4, -3.6) * mm, "end": v(-2.4, -3.6) * mm});
            skPoint(sketch, "E84.visualSharp", {"position": v(-3.6, 3.6) * mm});
            skArc(sketch, "E84.filletArc", {"start": v(-3.2, 3.6) * mm, "mid": v(-3.48, 3.48) * mm, "end": v(-3.6, 3.2) * mm});
            skPoint(sketch, "E85.visualSharp", {"position": v(-2.8, 3.6) * mm});
            skArc(sketch, "E85.filletArc", {"start": v(-2.8, 3.2) * mm, "mid": v(-2.92, 3.48) * mm, "end": v(-3.2, 3.6) * mm});
            skPoint(sketch, "E86.visualSharp", {"position": v(-2.8, -3.6) * mm});
            skArc(sketch, "E86.filletArc", {"start": v(-2.8, -3.2) * mm, "mid": v(-2.68, -3.48) * mm, "end": v(-2.4, -3.6) * mm});
            skPoint(sketch, "E87.visualSharp", {"position": v(-2, -3.6) * mm});
            skArc(sketch, "E87.filletArc", {"start": v(-2.4, -3.6) * mm, "mid": v(-2.12, -3.48) * mm, "end": v(-2, -3.2) * mm});
            skLineSegment(sketch, "E88", {"start": v(-2, 3.2) * mm, "end": v(-2, -3.2) * mm});
            skArc(sketch, "E89.1.0.0", {"start": v(-1.6, 3.6) * mm, "mid": v(-1.88, 3.48) * mm, "end": v(-2, 3.2) * mm});
            skArc(sketch, "E89.1.0.1", {"start": v(-1.2, 3.2) * mm, "mid": v(-1.32, 3.48) * mm, "end": v(-1.6, 3.6) * mm});
            skLineSegment(sketch, "E89.1.0.2", {"start": v(-1.2, 3.2) * mm, "end": v(-1.2, -3.2) * mm});
            skArc(sketch, "E89.1.0.3", {"start": v(-1.2, -3.2) * mm, "mid": v(-1.08, -3.48) * mm, "end": v(-0.8, -3.6) * mm});
            skArc(sketch, "E89.1.0.4", {"start": v(-0.8, -3.6) * mm, "mid": v(-0.52, -3.48) * mm, "end": v(-0.4, -3.2) * mm});
            skLineSegment(sketch, "E89.1.0.5", {"start": v(-0.4, 3.2) * mm, "end": v(-0.4, -3.2) * mm});
            skArc(sketch, "E89.2.0.0", {"start": v(0, 3.6) * mm, "mid": v(-0.28, 3.48) * mm, "end": v(-0.4, 3.2) * mm});
            skArc(sketch, "E89.2.0.1", {"start": v(0.4, 3.2) * mm, "mid": v(0.28, 3.48) * mm, "end": v(0, 3.6) * mm});
            skLineSegment(sketch, "E89.2.0.2", {"start": v(0.4, 3.2) * mm, "end": v(0.4, -3.2) * mm});
            skArc(sketch, "E89.2.0.3", {"start": v(0.4, -3.2) * mm, "mid": v(0.52, -3.48) * mm, "end": v(0.8, -3.6) * mm});
            skArc(sketch, "E89.2.0.4", {"start": v(0.8, -3.6) * mm, "mid": v(1.08, -3.48) * mm, "end": v(1.2, -3.2) * mm});
            skLineSegment(sketch, "E89.2.0.5", {"start": v(1.2, 3.2) * mm, "end": v(1.2, -3.2) * mm});
            skArc(sketch, "E89.3.0.0", {"start": v(1.6, 3.6) * mm, "mid": v(1.32, 3.48) * mm, "end": v(1.2, 3.2) * mm});
            skArc(sketch, "E89.3.0.1", {"start": v(2, 3.2) * mm, "mid": v(1.88, 3.48) * mm, "end": v(1.6, 3.6) * mm});
            skLineSegment(sketch, "E89.3.0.2", {"start": v(2, 3.2) * mm, "end": v(2, -3.2) * mm});
            skArc(sketch, "E89.3.0.3", {"start": v(2, -3.2) * mm, "mid": v(2.12, -3.48) * mm, "end": v(2.4, -3.6) * mm});
            skArc(sketch, "E89.3.0.4", {"start": v(2.4, -3.6) * mm, "mid": v(2.68, -3.48) * mm, "end": v(2.8, -3.2) * mm});
            skLineSegment(sketch, "E89.3.0.5", {"start": v(2.8, 3.2) * mm, "end": v(2.8, -3.2) * mm});
            skLineSegment(sketch, "E89.direction1", {"start": v(-2.4, -3.6) * mm, "end": v(-0.8, -3.6) * mm, "construction": true});
            skLineSegment(sketch, "E90", {"start": v(3.6, 3.6) * mm, "end": v(3.2, 3.6) * mm});
            skLineSegment(sketch, "E91", {"start": v(3.6, 3.6) * mm, "end": v(3.6, 3.2) * mm});
            skArc(sketch, "E92", {"start": v(2.8, 3.2) * mm, "mid": v(3.2, 3.6) * mm, "end": v(3.6, 3.2) * mm});
            skLineSegment(sketch, "E93", {"start": v(3.6, -3.6) * mm, "end": v(3.6, -2) * mm});
            skLineSegment(sketch, "E94", {"start": v(3.6, -2) * mm, "end": v(3.6, 3.2) * mm});
            skLineSegment(sketch, "E95", {"start": v(-3.6, 3.2) * mm, "end": v(-3.6, -5.2) * mm});
            skSolve(sketch);
        }
        {
            var Q0;
            Q0=qCreatedBy(id+"F8.planeOp",FACE);
            cPlane(context, id + "F10", {"entities" : qUnion([Q0]), "cplaneType" : CPlaneType.OFFSET, "offset" : 0.4 * mm, "width" : 150 * mm, "height" : 150 * mm});
        }
        {
            var Q0;
            Q0=qCreatedBy(id+"F10.planeOp",FACE);
            var sketch = newSketch(context, id + "F11", { "sketchPlane" : qUnion([Q0])});
            skLineSegment(sketch, "E96.bottom", {"start": v(2, 2) * mm, "end": v(-2, 2) * mm});
            skLineSegment(sketch, "E96.top", {"start": v(2, -2) * mm, "end": v(-1.6, -2) * mm});
            skLineSegment(sketch, "E96.left", {"start": v(2, -0.8) * mm, "end": v(2, -0.8) * mm});
            skLineSegment(sketch, "E96.right", {"start": v(-2, 2) * mm, "end": v(-2, -2) * mm});
            skPoint(sketch, "E96.middle", {"position": v(0, 0) * mm});
            skLineSegment(sketch, "E97", {"start": v(-2, -1.6) * mm, "end": v(-2, -1.6) * mm});
            skLineSegment(sketch, "E98", {"start": v(-1.6, -1.2) * mm, "end": v(1.6, -1.2) * mm});
            skLineSegment(sketch, "E99", {"start": v(-2, -1.2) * mm, "end": v(-2, -0.4) * mm});
            skLineSegment(sketch, "E100", {"start": v(-2, -0.4) * mm, "end": v(1.6, -0.4) * mm});
            skPoint(sketch, "E101.visualSharp", {"position": v(-2, -2) * mm});
            skArc(sketch, "E101.filletArc", {"start": v(-2, -1.6) * mm, "mid": v(-1.88, -1.88) * mm, "end": v(-1.6, -2) * mm});
            skPoint(sketch, "E102.visualSharp", {"position": v(-2, -1.2) * mm});
            skArc(sketch, "E102.filletArc", {"start": v(-1.6, -1.2) * mm, "mid": v(-1.88, -1.32) * mm, "end": v(-2, -1.6) * mm});
            skArc(sketch, "E103.filletArc", {"start": v(2, -0.8) * mm, "mid": v(1.88, -0.52) * mm, "end": v(1.6, -0.4) * mm});
            skArc(sketch, "E104.filletArc", {"start": v(1.6, -1.2) * mm, "mid": v(1.88, -1.08) * mm, "end": v(2, -0.8) * mm});
            skLineSegment(sketch, "E105", {"start": v(2, 2) * mm, "end": v(2, -2) * mm});
            skLineSegment(sketch, "E106", {"start": v(-1.6, -0.4) * mm, "end": v(1.6, -0.4) * mm});
            skArc(sketch, "E107.1.0.0", {"start": v(-1.6, 0.4) * mm, "mid": v(-1.88, 0.28) * mm, "end": v(-2, 0) * mm});
            skArc(sketch, "E107.1.0.1", {"start": v(-2, 0) * mm, "mid": v(-1.88, -0.28) * mm, "end": v(-1.6, -0.4) * mm});
            skLineSegment(sketch, "E107.1.0.2", {"start": v(-1.6, 0.4) * mm, "end": v(1.6, 0.4) * mm});
            skArc(sketch, "E107.1.0.3", {"start": v(1.6, 0.4) * mm, "mid": v(1.88, 0.52) * mm, "end": v(2, 0.8) * mm});
            skArc(sketch, "E107.1.0.4", {"start": v(2, 0.8) * mm, "mid": v(1.88, 1.08) * mm, "end": v(1.6, 1.2) * mm});
            skLineSegment(sketch, "E107.1.0.5", {"start": v(-1.6, 1.2) * mm, "end": v(1.6, 1.2) * mm});
            skLineSegment(sketch, "E107.direction1", {"start": v(-1.6, -2) * mm, "end": v(-1.6, -0.4) * mm, "construction": true});
            skLineSegment(sketch, "E108", {"start": v(-2, 2) * mm, "end": v(-2, 1.6) * mm});
            skLineSegment(sketch, "E109", {"start": v(-2, 2) * mm, "end": v(-1.6, 2) * mm});
            skArc(sketch, "E110", {"start": v(-1.6, 1.2) * mm, "mid": v(-2, 1.6) * mm, "end": v(-1.6, 2) * mm});
            skLineSegment(sketch, "E111", {"start": v(1.2, 2) * mm, "end": v(-1.6, 2) * mm});
            skLineSegment(sketch, "E112", {"start": v(-1.6, -2) * mm, "end": v(3.6, -2) * mm});
            skSolve(sketch);
        }
        {
            var Q0;
            Q0=qCreatedBy(id+"F10.planeOp",FACE);
            cPlane(context, id + "F12", {"entities" : qUnion([Q0]), "cplaneType" : CPlaneType.OFFSET, "offset" : 0.4 * mm, "width" : 150 * mm, "height" : 150 * mm});
        }
        {
            var Q0;
            Q0=qCreatedBy(id+"F12.planeOp",FACE);
            var sketch = newSketch(context, id + "F13", { "sketchPlane" : qUnion([Q0])});
            skCircle(sketch, "E113", {"center": v(0, 0) * mm, "radius": 0.4 * mm});
            skLineSegment(sketch, "E114", {"start": v(0, 0) * mm, "end": v(0, 0.4) * mm});
            skLineSegment(sketch, "E115", {"start": v(0, 0.4) * mm, "end": v(0.8, 0.4) * mm});
            skLineSegment(sketch, "E116", {"start": v(1.2, 0.8) * mm, "end": v(1.2, 2) * mm});
            skPoint(sketch, "E117.visualSharp", {"position": v(1.2, 0.4) * mm});
            skArc(sketch, "E117.filletArc", {"start": v(0.8, 0.4) * mm, "mid": v(1.08, 0.52) * mm, "end": v(1.2, 0.8) * mm});
            skLineSegment(sketch, "E118", {"start": v(0, 0) * mm, "end": v(0, -0.4) * mm});
            skSolve(sketch);
        }
        {
            var Q0;
            Q0=sQuery(id+"F3.wireOp",EDGE,"E36");
            var Q1;
            Q1=sQuery(id+"F3.wireOp",VERTEX,"E36.end");
            cPlane(context, id + "F14", {"entities" : qUnion([Q0, Q1]), "cplaneType" : CPlaneType.LINE_POINT, "offset" : 25 * mm, "width" : 150 * mm, "height" : 150 * mm});
        }
        {
            var Q0;
            Q0=qCreatedBy(id+"F14.planeOp",FACE);
            var sketch = newSketch(context, id + "F15", { "sketchPlane" : qUnion([Q0])});
            skLineSegment(sketch, "E119", {"start": v(-8.4, 0.62) * mm, "end": v(-8.4, 0.21) * mm});
            skSolve(sketch);
        }
        {
            var Q0;
            Q0=sQuery(id+"F5.wireOp",VERTEX,"E55.end");
            var Q1;
            Q1=sQuery(id+"F5.wireOp",EDGE,"E55");
            cPlane(context, id + "F16", {"entities" : qUnion([Q0, Q1]), "cplaneType" : CPlaneType.LINE_POINT, "offset" : 25 * mm, "width" : 150 * mm, "height" : 150 * mm});
        }
        {
            var Q0;
            Q0=qCreatedBy(id+"F16.planeOp",FACE);
            var sketch = newSketch(context, id + "F17", { "sketchPlane" : qUnion([Q0])});
            skLineSegment(sketch, "E120", {"start": v(-6.8, 1.03) * mm, "end": v(-6.8, 0.62) * mm});
            skSolve(sketch);
        }
        {
            var Q0;
            Q0=sQuery(id+"F7.wireOp",EDGE,"E76");
            var Q1;
            Q1=sQuery(id+"F7.wireOp",VERTEX,"E76.end");
            cPlane(context, id + "F18", {"entities" : qUnion([Q0, Q1]), "cplaneType" : CPlaneType.LINE_POINT, "offset" : 25 * mm, "width" : 150 * mm, "height" : 150 * mm});
        }
        {
            var Q0;
            Q0=qCreatedBy(id+"F18.planeOp",FACE);
            var sketch = newSketch(context, id + "F19", { "sketchPlane" : qUnion([Q0])});
            skLineSegment(sketch, "E121", {"start": v(-5.2, 1.44) * mm, "end": v(-5.2, 1.03) * mm});
            skSolve(sketch);
        }
        {
            var Q0;
            Q0=sQuery(id+"F9.wireOp",EDGE,"E95");
            var Q1;
            Q1=sQuery(id+"F9.wireOp",VERTEX,"E95.end");
            cPlane(context, id + "F20", {"entities" : qUnion([Q0, Q1]), "cplaneType" : CPlaneType.LINE_POINT, "offset" : 25 * mm, "width" : 150 * mm, "height" : 150 * mm});
        }
        {
            var Q0;
            Q0=qCreatedBy(id+"F20.planeOp",FACE);
            var sketch = newSketch(context, id + "F21", { "sketchPlane" : qUnion([Q0])});
            skLineSegment(sketch, "E122", {"start": v(-3.6, 1.85) * mm, "end": v(-3.6, 1.44) * mm});
            skSolve(sketch);
        }
        {
            var Q0;
            Q0=sQuery(id+"F11.wireOp",EDGE,"E112");
            var Q1;
            Q1=sQuery(id+"F11.wireOp",VERTEX,"E112.end");
            cPlane(context, id + "F22", {"entities" : qUnion([Q0, Q1]), "cplaneType" : CPlaneType.LINE_POINT, "offset" : 25 * mm, "width" : 150 * mm, "height" : 150 * mm});
        }
        {
            var Q0;
            Q0=qCreatedBy(id+"F22.planeOp",FACE);
            var sketch = newSketch(context, id + "F23", { "sketchPlane" : qUnion([Q0])});
            skLineSegment(sketch, "E123", {"start": v(-2, 2.26) * mm, "end": v(-2, 1.85) * mm});
            skSolve(sketch);
        }
        {
            var Q0;
            Q0=sQuery(id+"F13.wireOp",EDGE,"E116");
            var Q1;
            Q1=sQuery(id+"F13.wireOp",VERTEX,"E116.end");
            cPlane(context, id + "F24", {"entities" : qUnion([Q0, Q1]), "cplaneType" : CPlaneType.LINE_POINT, "offset" : 25 * mm, "width" : 150 * mm, "height" : 150 * mm});
        }
        {
            var Q0;
            Q0=qCreatedBy(id+"F24.planeOp",FACE);
            var sketch = newSketch(context, id + "F25", { "sketchPlane" : qUnion([Q0])});
            skLineSegment(sketch, "E124", {"start": v(-1.2, 2.67) * mm, "end": v(-1.2, 2.26) * mm});
            skSolve(sketch);
        }
        {
            var Q0;
            Q0=sQuery(id+"F1.wireOp",EDGE,"E18");
            var Q1;
            Q1=sQuery(id+"F1.wireOp",VERTEX,"E18.end");
            cPlane(context, id + "F26", {"entities" : qUnion([Q0, Q1]), "cplaneType" : CPlaneType.LINE_POINT, "offset" : 25 * mm, "width" : 150 * mm, "height" : 150 * mm});
        }
        {
            var Q0;
            Q0=qCreatedBy(id+"F26.planeOp",FACE);
            var sketch = newSketch(context, id + "F27", { "sketchPlane" : qUnion([Q0])});
            skCircle(sketch, "E125", {"center": v(-10, 0.21) * mm, "radius": 0.2 * mm});
            skSolve(sketch);
        }
        {
            var Q0;
            Q0=sQuery(id+"F13.wireOp",VERTEX,"E118.end");
            var Q1;
            Q1=sQuery(id+"F13.wireOp",EDGE,"E113");
            cPlane(context, id + "F28", {"entities" : qUnion([Q0, Q1]), "cplaneType" : CPlaneType.CURVE_POINT, "offset" : 25 * mm, "width" : 150 * mm, "height" : 150 * mm});
        }
        {
            var Q0;
            Q0=qCreatedBy(id+"F28.planeOp",FACE);
            var sketch = newSketch(context, id + "F29", { "sketchPlane" : qUnion([Q0])});
            skCircle(sketch, "E126", {"center": v(-0.4, 2.67) * mm, "radius": 0.2 * mm});
            skSolve(sketch);
        }
        {
            var Q0;
            Q0=makeQuery(id+"F29.imprint","IMPRINT",FACE,{"disambiguationData":[TD([[makeQuery(id+"F29.imprint","IMPRINT",EDGE,{"derivedFrom":sQuery(id+"F29.wireOp",EDGE,"E126")}),1.0]])]});
            var Q1;
            Q1=sQuery(id+"F13.wireOp",EDGE,"E113");
            sweep(context, id + "F30", {"profiles" : qUnion([Q0]), "path" : qUnion([Q1])});
        }
    });
